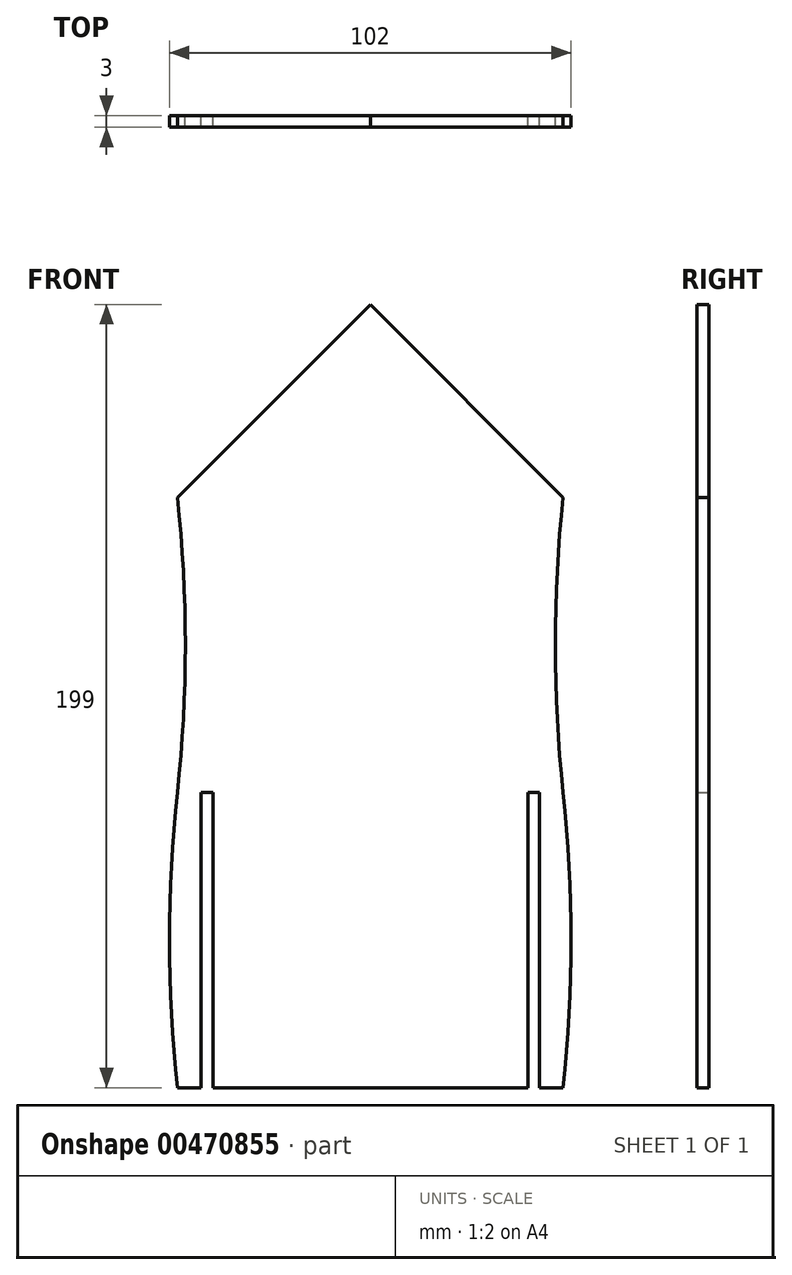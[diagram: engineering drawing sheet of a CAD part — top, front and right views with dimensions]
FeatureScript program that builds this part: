
annotation { "Feature Type Name" : "Feature", "Feature Type Description" : "" }
export const myFeature = defineFeature(function(context is Context, id is Id, definition is map)
    precondition{}
    {
        {
            assignVariable(context, id + "F0", {"name" : "WoodWidth", "anyValue" : 3});
        }
        {
            var Q0;
            Q0=qCreatedBy(makeId("Front.planeOp"),FACE);
            var sketch = newSketch(context, id + "F1", { "sketchPlane" : qUnion([Q0])});
            skLineSegment(sketch, "E0.bottom", {"start": v(49, -75) * mm, "end": v(-49, -75) * mm});
            skLineSegment(sketch, "E0.top", {"start": v(49, 75) * mm, "end": v(-49, 75) * mm});
            skLineSegment(sketch, "E0.left", {"start": v(49, -75) * mm, "end": v(49, 75) * mm});
            skLineSegment(sketch, "E0.right", {"start": v(-49, -75) * mm, "end": v(-49, 75) * mm});
            skPoint(sketch, "E0.middle", {"position": v(0, 0) * mm});
            skLineSegment(sketch, "E1.bottom", {"start": v(-43, -75) * mm, "end": v(-40, -75) * mm});
            skLineSegment(sketch, "E1.top", {"start": v(-43, 0) * mm, "end": v(-40, 0) * mm});
            skLineSegment(sketch, "E1.left", {"start": v(-43, -75) * mm, "end": v(-43, 0) * mm});
            skLineSegment(sketch, "E1.right", {"start": v(-40, -75) * mm, "end": v(-40, 0) * mm});
            skLineSegment(sketch, "E2.bottom", {"start": v(40, -75) * mm, "end": v(43, -75) * mm});
            skLineSegment(sketch, "E2.top", {"start": v(40, 0) * mm, "end": v(43, 0) * mm});
            skLineSegment(sketch, "E2.left", {"start": v(40, -75) * mm, "end": v(40, 0) * mm});
            skLineSegment(sketch, "E2.right", {"start": v(43, -75) * mm, "end": v(43, 0) * mm});
            skLineSegment(sketch, "E3.bottom", {"start": v(-40, -75) * mm, "end": v(-28, -75) * mm});
            skLineSegment(sketch, "E3.top", {"start": v(-40, -78) * mm, "end": v(-28, -78) * mm});
            skLineSegment(sketch, "E3.left", {"start": v(-40, -75) * mm, "end": v(-40, -78) * mm});
            skLineSegment(sketch, "E3.right", {"start": v(-28, -75) * mm, "end": v(-28, -78) * mm});
            skLineSegment(sketch, "E4.bottom", {"start": v(40, -75) * mm, "end": v(28, -75) * mm});
            skLineSegment(sketch, "E4.top", {"start": v(40, -78) * mm, "end": v(28, -78) * mm});
            skLineSegment(sketch, "E4.left", {"start": v(40, -75) * mm, "end": v(40, -78) * mm});
            skLineSegment(sketch, "E4.right", {"start": v(28, -75) * mm, "end": v(28, -78) * mm});
            skLineSegment(sketch, "E5.bottom", {"start": v(-49, -75) * mm, "end": v(-43, -75) * mm});
            skLineSegment(sketch, "E5.top", {"start": v(-49, -78) * mm, "end": v(-43, -78) * mm});
            skLineSegment(sketch, "E5.left", {"start": v(-49, -75) * mm, "end": v(-49, -78) * mm});
            skLineSegment(sketch, "E5.right", {"start": v(-43, -75) * mm, "end": v(-43, -78) * mm});
            skLineSegment(sketch, "E6.bottom", {"start": v(43, -75) * mm, "end": v(49, -75) * mm});
            skLineSegment(sketch, "E6.top", {"start": v(43, -78) * mm, "end": v(49, -78) * mm});
            skLineSegment(sketch, "E6.left", {"start": v(43, -75) * mm, "end": v(43, -78) * mm});
            skLineSegment(sketch, "E6.right", {"start": v(49, -75) * mm, "end": v(49, -78) * mm});
            skLineSegment(sketch, "E7", {"start": v(-49, 75) * mm, "end": v(0, 124) * mm});
            skLineSegment(sketch, "E8", {"start": v(0, 124) * mm, "end": v(49, 75) * mm});
            skArc(sketch, "E9", {"start": v(-49, 0) * mm, "mid": v(-51, -37.5) * mm, "end": v(-49, -75) * mm});
            skArc(sketch, "E10", {"start": v(-49, 0) * mm, "mid": v(-47, 37.5) * mm, "end": v(-49, 75) * mm});
            skArc(sketch, "E11", {"start": v(49, 75) * mm, "mid": v(47, 37.5) * mm, "end": v(49, 0) * mm});
            skArc(sketch, "E12", {"start": v(49, -75) * mm, "mid": v(51, -37.5) * mm, "end": v(49, 0) * mm});
            skSolve(sketch);
        }
        {
            var Q0;
            Q0=makeQuery(id+"F1.imprint","IMPRINT",FACE,{"disambiguationData":[TD([[makeQuery(id+"F1.imprint","IMPRINT",EDGE,{"derivedFrom":sQuery(id+"F1.wireOp",EDGE,"E0.top")}),-1.0]])]});
            var Q1;
            Q1=makeQuery(id+"F1.imprint","IMPRINT",FACE,{"disambiguationData":[TD([[makeQuery(id+"F1.imprint","IMPRINT",EDGE,{"derivedFrom":sQuery(id+"F1.wireOp",EDGE,"E0.bottom")}),-1.0]])]});
            var Q2;
            Q2=makeQuery(id+"F1.imprint","IMPRINT",FACE,{"disambiguationData":[TD([[makeQuery(id+"F1.imprint","IMPRINT",EDGE,{"derivedFrom":sQuery(id+"F1.wireOp",EDGE,"E5.bottom")}),-1.0]])]});
            var Q3;
            Q3=makeQuery(id+"F1.imprint","IMPRINT",FACE,{"disambiguationData":[TD([[makeQuery(id+"F1.imprint","IMPRINT",EDGE,{"derivedFrom":sQuery(id+"F1.wireOp",EDGE,"E3.bottom")}),-1.0]])]});
            var Q4;
            Q4=makeQuery(id+"F1.imprint","IMPRINT",FACE,{"disambiguationData":[TD([[makeQuery(id+"F1.imprint","IMPRINT",EDGE,{"derivedFrom":sQuery(id+"F1.wireOp",EDGE,"E4.bottom")}),1.0]])]});
            var Q5;
            Q5=makeQuery(id+"F1.imprint","IMPRINT",FACE,{"disambiguationData":[TD([[makeQuery(id+"F1.imprint","IMPRINT",EDGE,{"derivedFrom":sQuery(id+"F1.wireOp",EDGE,"E6.bottom")}),-1.0]])]});
            var Q6;
            {var subQ0=sQuery(id+"F1.wireOp",EDGE,"E9");Q6=makeQuery(id+"F1.imprint","IMPRINT",FACE,{"disambiguationData":[TD([[makeQuery(id+"F1.imprint","IMPRINT",EDGE,{"derivedFrom":subQ0}),1.0]])]});}
            var Q7;
            {var subQ0=sQuery(id+"F1.wireOp",EDGE,"E12");Q7=makeQuery(id+"F1.imprint","IMPRINT",FACE,{"disambiguationData":[TD([[makeQuery(id+"F1.imprint","IMPRINT",EDGE,{"derivedFrom":subQ0}),1.0]])]});}
            extrude(context, id + "F2", {"entities" : qUnion([Q0, Q1, Q2, Q3, Q4, Q5, Q6, Q7]), "depth" : (getVariable(context, 'WoodWidth')) * mm});
        }
    });
